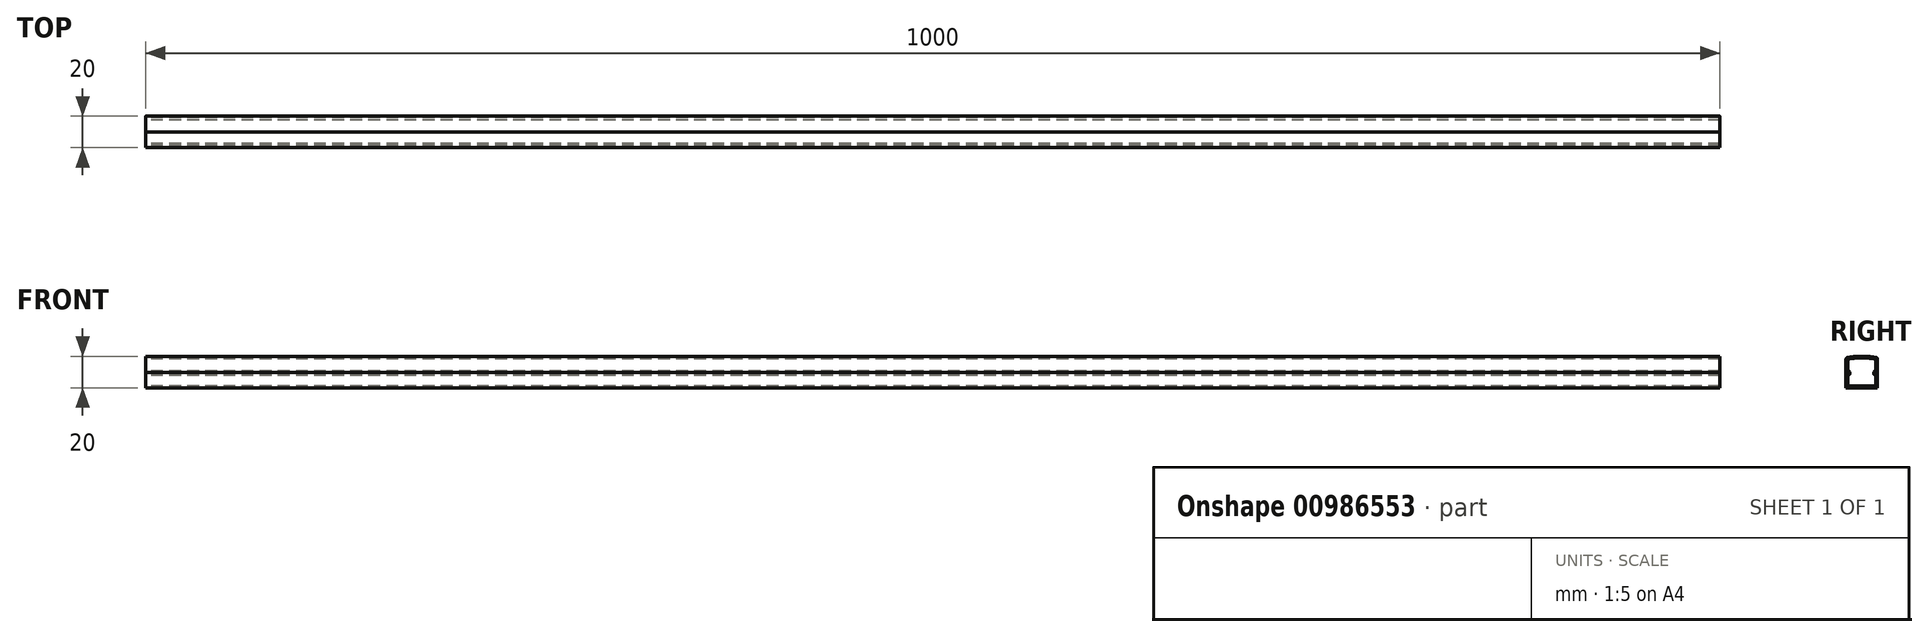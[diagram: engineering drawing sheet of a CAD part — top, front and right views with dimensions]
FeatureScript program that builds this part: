
annotation { "Feature Type Name" : "Feature", "Feature Type Description" : "" }
export const myFeature = defineFeature(function(context is Context, id is Id, definition is map)
    precondition{}
    {
        {
            var Q0;
            Q0=qCreatedBy(makeId("Right.planeOp"),FACE);
            var sketch = newSketch(context, id + "F0", { "sketchPlane" : qUnion([Q0])});
            skLineSegment(sketch, "E0.bottom", {"start": v(-10, -10) * mm, "end": v(10, -10) * mm});
            skLineSegment(sketch, "E0.top", {"start": v(-10, 10) * mm, "end": v(10, 10) * mm});
            skLineSegment(sketch, "E0.left", {"start": v(-10, -10) * mm, "end": v(-10, 10) * mm});
            skLineSegment(sketch, "E0.right", {"start": v(10, -10) * mm, "end": v(10, 10) * mm});
            skPoint(sketch, "E0.middle", {"position": v(0, 0) * mm});
            skSolve(sketch);
        }
        {
            var Q0;
            Q0=qCreatedBy(makeId("Right.planeOp"),FACE);
            var sketch = newSketch(context, id + "F1", { "sketchPlane" : qUnion([Q0])});
            skLineSegment(sketch, "E1.0", {"start": v(0, -10) * mm, "end": v(10, -10) * mm});
            skLineSegment(sketch, "E1.3", {"start": v(10, -10) * mm, "end": v(10, -0.2) * mm});
            skPoint(sketch, "E1.4", {"position": v(0, 0) * mm});
            skLineSegment(sketch, "E2.0", {"start": v(9, -9) * mm, "end": v(9, -2.2) * mm});
            skLineSegment(sketch, "E2.1", {"start": v(0.13, -9) * mm, "end": v(9, -9) * mm});
            skLineSegment(sketch, "E3", {"start": v(10, -0.2) * mm, "end": v(9, -0.2) * mm});
            skArc(sketch, "E4", {"start": v(9, -0.2) * mm, "mid": v(8.5, -0.7) * mm, "end": v(9, -1.2) * mm});
            skArc(sketch, "E5", {"start": v(9, -2.2) * mm, "mid": v(9.5, -1.7) * mm, "end": v(9, -1.2) * mm});
            skLineSegment(sketch, "E6", {"start": v(0.13, -9) * mm, "end": v(0, -10) * mm});
            skPoint(sketch, "E1.1.end.orphan", {"position": v(10, 10) * mm});
            skPoint(sketch, "E1.1.start.orphan", {"position": v(-10, 10) * mm});
            skPoint(sketch, "E1.2.end.orphan", {"position": v(-10, 10) * mm});
            skPoint(sketch, "E1.2.start.orphan", {"position": v(-10, -10) * mm});
            skPoint(sketch, "E7.orphan", {"position": v(-8.75, -9) * mm});
            skSolve(sketch);
        }
        {
            var Q0;
            Q0 = qSketchRegion(id + "F1", true);
            extrude(context, id + "F2", {"entities" : qUnion([Q0]), "depth" : 1000 * mm, "offsetDistance" : 25 * mm});
        }
        {
            var Q0;
            Q0=qCreatedBy(makeId("Right.planeOp"),FACE);
            var sketch = newSketch(context, id + "F3", { "sketchPlane" : qUnion([Q0])});
            skPoint(sketch, "E8.2", {"position": v(0, 0) * mm});
            skLineSegment(sketch, "E8.5", {"start": v(10, -0.2) * mm, "end": v(9, -0.2) * mm});
            skArc(sketch, "E8.6", {"start": v(9, -0.2) * mm, "mid": v(8.5, -0.7) * mm, "end": v(9, -1.2) * mm});
            skArc(sketch, "E8.7", {"start": v(9, -2.2) * mm, "mid": v(9.5, -1.7) * mm, "end": v(9, -1.2) * mm});
            skPoint(sketch, "E8.9", {"position": v(10, 10) * mm});
            skPoint(sketch, "E8.10", {"position": v(10, 10) * mm});
            skPoint(sketch, "E8.11", {"position": v(-10, 10) * mm});
            skPoint(sketch, "E8.12", {"position": v(-10, 10) * mm});
            skPoint(sketch, "E8.13", {"position": v(-10, -10) * mm});
            skPoint(sketch, "E8.14", {"position": v(-8.75, -9) * mm});
            skPoint(sketch, "E8.15", {"position": v(-10, -10) * mm});
            skPoint(sketch, "E8.1.end.orphan", {"position": v(10, -0.2) * mm});
            skPoint(sketch, "E8.1.start.orphan", {"position": v(10, -10) * mm});
            skPoint(sketch, "E8.3.end.orphan", {"position": v(9, -2.2) * mm});
            skPoint(sketch, "E8.3.start.orphan", {"position": v(9, -9) * mm});
            skPoint(sketch, "E8.4.end.orphan", {"position": v(9, -9) * mm});
            skPoint(sketch, "E8.4.start.orphan", {"position": v(0.13, -9) * mm});
            skPoint(sketch, "E8.0.end.orphan", {"position": v(10, -10) * mm});
            skPoint(sketch, "E8.0.start.orphan", {"position": v(0, -10) * mm});
            skPoint(sketch, "E8.8.end.orphan", {"position": v(0, -10) * mm});
            skPoint(sketch, "E8.8.start.orphan", {"position": v(0.13, -9) * mm});
            skLineSegment(sketch, "E9", {"start": v(10, -0.2) * mm, "end": v(10, 8.17) * mm});
            skArc(sketch, "E10", {"start": v(9.18, 9.15) * mm, "mid": v(4.61, 9.79) * mm, "end": v(0, 10) * mm});
            skLineSegment(sketch, "E11", {"start": v(0, 10) * mm, "end": v(-15.57, 10) * mm, "construction": true});
            skPoint(sketch, "E12.visualSharp", {"position": v(10, 8.99) * mm});
            skArc(sketch, "E12.filletArc", {"start": v(10, 8.17) * mm, "mid": v(9.77, 8.8) * mm, "end": v(9.18, 9.15) * mm});
            skArc(sketch, "E13.0", {"start": v(9, 8.17) * mm, "mid": v(4.52, 8.8) * mm, "end": v(0, 9) * mm});
            skLineSegment(sketch, "E13.1", {"start": v(9, 0.8) * mm, "end": v(9, 8.17) * mm});
            skArc(sketch, "E13.2", {"start": v(9, 0.8) * mm, "mid": v(7.5, -0.7) * mm, "end": v(9, -2.2) * mm});
            skLineSegment(sketch, "E14", {"start": v(0, 10) * mm, "end": v(0, 9) * mm});
            skSolve(sketch);
        }
        {
            var Q0;
            Q0 = qSketchRegion(id + "F3", true);
            extrude(context, id + "F4", {"entities" : qUnion([Q0]), "depth" : 1000 * mm, "offsetDistance" : 25 * mm});
        }
        {
            var Q0;
            Q0=makeQuery(id+"F2.opExtrude","SWEPT_BODY",BODY,{"disambiguationData":[OSD([sQuery(id+"F1.wireOp",EDGE,"E1.0"),sQuery(id+"F1.wireOp",EDGE,"E1.3"),sQuery(id+"F1.wireOp",EDGE,"E2.0"),sQuery(id+"F1.wireOp",EDGE,"E2.1"),sQuery(id+"F1.wireOp",EDGE,"E3"),sQuery(id+"F1.wireOp",EDGE,"E4"),sQuery(id+"F1.wireOp",EDGE,"E5"),sQuery(id+"F1.wireOp",EDGE,"E6")])]});
            var Q1;
            Q1=qCreatedBy(makeId("Front.planeOp"),FACE);
            mirror(context, id + "F5", {"operationType" : NewBodyOperationType.ADD, "entities" : qUnion([Q0]), "mirrorPlane" : qUnion([Q1])});
        }
        {
            var Q0;
            Q0=makeQuery(id+"F4.opExtrude","SWEPT_BODY",BODY,{"disambiguationData":[OSD([sQuery(id+"F3.wireOp",EDGE,"E8.5"),sQuery(id+"F3.wireOp",EDGE,"E8.6"),sQuery(id+"F3.wireOp",EDGE,"E8.7"),sQuery(id+"F3.wireOp",EDGE,"E9"),sQuery(id+"F3.wireOp",EDGE,"E10"),sQuery(id+"F3.wireOp",EDGE,"E12.filletArc"),sQuery(id+"F3.wireOp",EDGE,"E13.0"),sQuery(id+"F3.wireOp",EDGE,"E13.1"),sQuery(id+"F3.wireOp",EDGE,"E13.2"),sQuery(id+"F3.wireOp",EDGE,"E14")])]});
            var Q1;
            Q1=qCreatedBy(makeId("Front.planeOp"),FACE);
            mirror(context, id + "F6", {"operationType" : NewBodyOperationType.ADD, "entities" : qUnion([Q0]), "mirrorPlane" : qUnion([Q1])});
        }
    });
